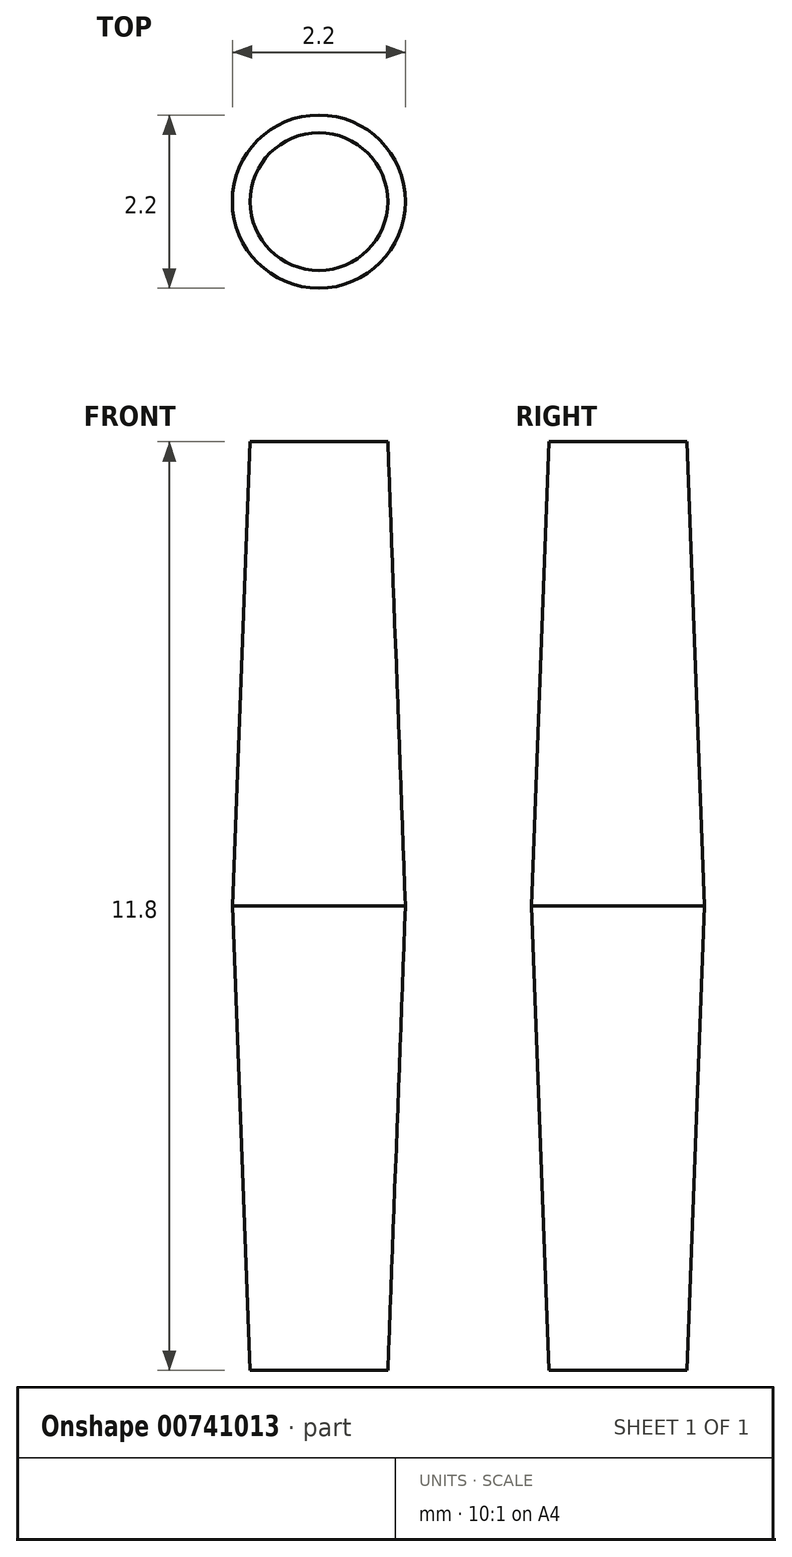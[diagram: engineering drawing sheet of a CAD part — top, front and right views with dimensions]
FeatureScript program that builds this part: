
annotation { "Feature Type Name" : "Feature", "Feature Type Description" : "" }
export const myFeature = defineFeature(function(context is Context, id is Id, definition is map)
    precondition{}
    {
        {
            var Q0;
            Q0=qCreatedBy(makeId("Front.planeOp"),FACE);
            var sketch = newSketch(context, id + "F0", { "sketchPlane" : qUnion([Q0])});
            skLineSegment(sketch, "E0", {"start": v(0, 0) * mm, "end": v(-1.1, 0) * mm, "construction": true});
            skLineSegment(sketch, "E1", {"start": v(0, 5.9) * mm, "end": v(-0.88, 5.9) * mm});
            skLineSegment(sketch, "E2", {"start": v(-0.88, 5.9) * mm, "end": v(-1.1, 0) * mm});
            skLineSegment(sketch, "E3.MirrorCS", {"start": v(0, -5.9) * mm, "end": v(-0.88, -5.9) * mm});
            skLineSegment(sketch, "E4.MirrorCS", {"start": v(-0.88, -5.9) * mm, "end": v(-1.1, 0) * mm});
            skLineSegment(sketch, "E5", {"start": v(0, -5.9) * mm, "end": v(0, 5.9) * mm});
            skSolve(sketch);
        }
        {
            var Q0;
            Q0=makeQuery(id+"F0.imprint","IMPRINT",FACE,{"disambiguationData":[TD([[makeQuery(id+"F0.imprint","IMPRINT",EDGE,{"derivedFrom":sQuery(id+"F0.wireOp",EDGE,"E1")}),1.0]])]});
            var Q1;
            Q1=sQuery(id+"F0.wireOp",EDGE,"E5");
            revolve(context, id + "F1", {"surfaceOperationType" : NewSurfaceOperationType.NEW, "entities" : qUnion([Q0]), "axis" : qUnion([Q1]), "revolveType" : RevolveType.FULL, "oppositeDirection" : true});
        }
    });
